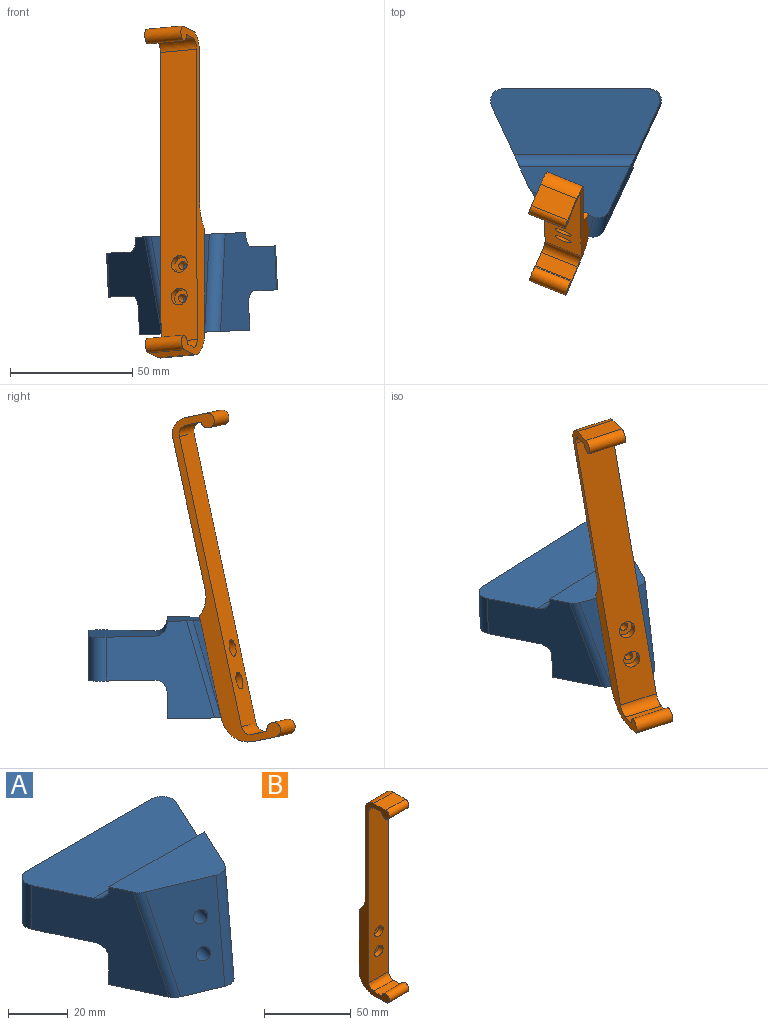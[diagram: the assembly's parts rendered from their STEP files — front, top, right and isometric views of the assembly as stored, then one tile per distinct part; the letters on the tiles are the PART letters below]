
ASSEMBLY  parts=2 mates=1
PART A: 20 faces, bbox 69.3x60.6x42.1 mm
  f0: plane 69.3x27mm, normal (0,0,1), area 1656.8mm2, adj f1,f3,f4,f16,f17,f19
  f1: plane 44.28x40mm, normal (-0.91,-0.42,0), area 1109.5mm2, adj f0,f2,f5,f6,f7,f9,f14,f16
  f2: plane 69.3x27mm, normal (0,0,-1), area 1656.8mm2, adj f1,f3,f4,f16,f17,f18
  f3: plane 50.54x40mm, normal (0.91,-0.42,0), area 1467.5mm2, adj f0,f2,f5,f6,f7,f9,f15,f17
  f4: plane 59.3x18mm, normal (0,1,0), area 1067.5mm2, adj f0,f2,f16,f17
  f5: plane 45.16x11mm, normal (0,1,0), area 496.7mm2, adj f1,f3,f6,f18
  f6: plane 45.16x28.63mm, normal (0,0,-1), area 856mm2, adj f1,f3,f5,f8,f14,f15
  f7: plane 45.16x20.89mm, normal (0,0,1), area 619.1mm2, adj f1,f3,f8,f9,f14,f15
  f8: plane 40x23.8mm, normal (-0.37,-0.9,0.21), area 813.3mm2, adj f6,f7,f11,f13,f14,f15
  f9: plane 45.16x1mm, normal (0,1,0), area 45.2mm2, adj f1,f3,f7,f19
  f10: cone r=0mm half-angle=59deg, axis (-0.37,-0.9,0.21), area 24.8mm2, adj f11
  f11: cylinder r=2.6mm len=13.07mm, axis (-0.37,-0.9,0.21), area 196mm2, adj f8,f10
  f12: cone r=0mm half-angle=59deg, axis (-0.37,-0.9,0.21), area 24.8mm2, adj f13
  f13: cylinder r=2.6mm len=13.07mm, axis (-0.37,-0.9,0.21), area 196mm2, adj f8,f12
  f14: cylinder r=5mm len=42.09mm, axis (-0.13,0.27,0.95), area 160.5mm2, adj f1,f6,f7,f8
  f15: cylinder r=5mm len=42.09mm, axis (0.09,0.19,0.98), area 312.6mm2, adj f3,f6,f7,f8
  f16: cylinder r=5mm len=18mm, axis (0,0,1), area 180.6mm2, adj f0,f1,f2,f4
  f17: cylinder r=5mm len=18mm, axis (0,0,1), area 180.6mm2, adj f0,f2,f3,f4
  f18: cylinder r=5mm len=49.82mm, axis (-1,0,0), area 368mm2, adj f1,f2,f3,f5
  f19: cylinder r=5mm len=49.82mm, axis (1,0,0), area 368mm2, adj f0,f1,f3,f9
PART B: 24 faces, bbox 16x24.7x135.5 mm
  f0: plane 63.75x16mm, normal (0,1,0), area 1020.1mm2, adj f9,f10,f13,f15
  f1: plane 16x9.7mm, normal (0,0,1), area 155.2mm2, adj f2,f9,f10,f13
  f2: cylinder r=3mm len=16mm, axis (-1,0,0), area 217.1mm2, adj f1,f9,f10,f16
  f3: plane 16x6.07mm, normal (0,0,-1), area 97.1mm2, adj f9,f10,f11,f16
  f4: plane 121.5x16mm, normal (0,-1,0), area 1867mm2, adj f9,f10,f11,f12,f20,f23
  f5: plane 16x6.07mm, normal (0,0,1), area 97.1mm2, adj f9,f10,f12,f17
  f6: cylinder r=3mm len=16mm, axis (-1,0,0), area 217.1mm2, adj f7,f9,f10,f17
  f7: plane 16x9.7mm, normal (0,0,-1), area 155.2mm2, adj f6,f9,f10,f14
  f8: plane 43x16mm, normal (0,1,0), area 669.8mm2, adj f9,f10,f14,f15,f18,f21
  f9: plane 135.5x24.7mm, normal (1,0,0), area 786.3mm2, adj f0,f1,f2,f3,f4,f5,f6,f7
  f10: plane 135.5x24.7mm, normal (-1,0,0), area 786.3mm2, adj f0,f1,f2,f3,f4,f5,f6,f7
  f11: cylinder r=4mm len=16mm, axis (1,0,0), area 100.5mm2, adj f3,f4,f9,f10
  f12: cylinder r=4mm len=16mm, axis (-1,0,0), area 100.5mm2, adj f4,f5,f9,f10
  f13: cylinder r=7mm len=16mm, axis (1,0,0), area 175.9mm2, adj f0,f1,f9,f10
  f14: cylinder r=12mm len=16mm, axis (-1,0,0), area 301.6mm2, adj f7,f8,f9,f10
  f15: cylinder r=12mm len=16mm, axis (1,0,0), area 182mm2, adj f0,f8,f9,f10
  f16: cylinder r=0.7mm len=16mm, axis (-1,0,0), area 15.5mm2, adj f2,f3,f9,f10
  f17: cylinder r=0.7mm len=16mm, axis (-1,0,0), area 15.5mm2, adj f5,f6,f9,f10
  f18: cylinder r=1.7mm len=4.5mm, axis (0,-1,0), area 48.1mm2, adj f8,f19
  f19: plane 7x7mm, normal (0,-1,0), area 29.4mm2, adj f18,f20
  f20: cylinder r=3.5mm len=7mm, axis (0,-1,0), area 77mm2, adj f4,f19
  f21: cylinder r=1.7mm len=4.5mm, axis (0,-1,0), area 48.1mm2, adj f8,f22
  f22: plane 7x7mm, normal (0,-1,0), area 29.4mm2, adj f21,f23
  f23: cylinder r=3.5mm len=7mm, axis (0,-1,0), area 77mm2, adj f4,f22
PLACE A rot(axis=(0,-1,0),2.5deg) t=(36.44,-82.13,27.25)mm
PLACE B rot(axis=(-0.47,-0.1,-0.88),25.5deg) t=(24.8,-146.81,-5.25)mm
MATE revolute B.f8 <-> A.f8  axis (0.38,0.9,-0.19) through (37.57,-139.31,-17.27)mm
